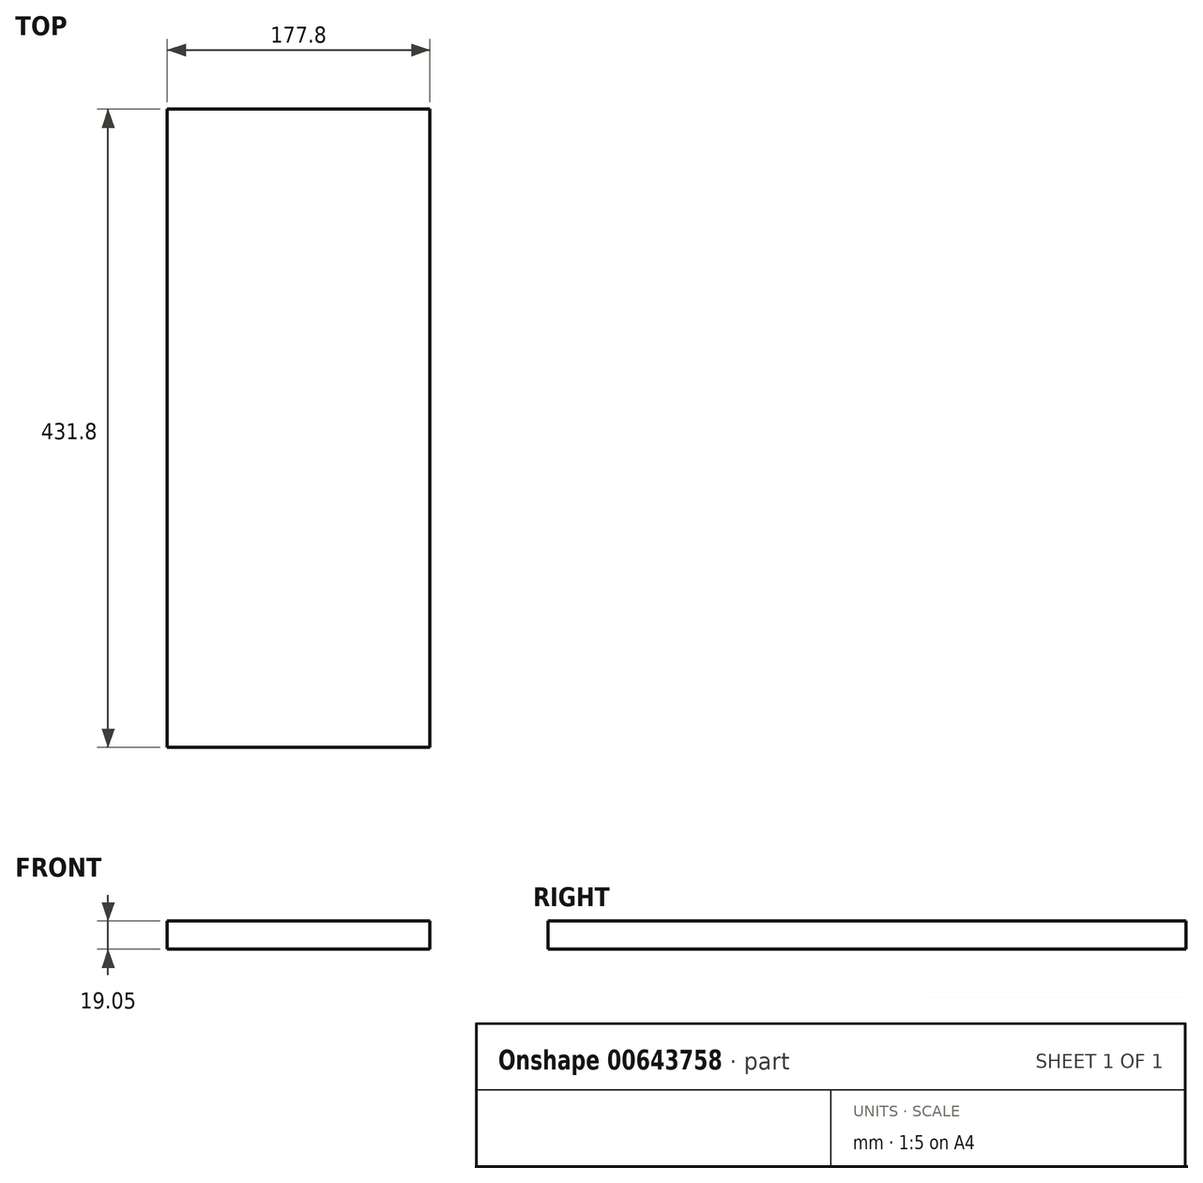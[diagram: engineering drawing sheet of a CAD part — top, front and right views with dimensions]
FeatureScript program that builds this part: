
annotation { "Feature Type Name" : "Feature", "Feature Type Description" : "" }
export const myFeature = defineFeature(function(context is Context, id is Id, definition is map)
    precondition{}
    {
        {
            var Q0;
            Q0=qCreatedBy(makeId("Top.planeOp"),FACE);
            var sketch = newSketch(context, id + "F0", { "sketchPlane" : qUnion([Q0])});
            skLineSegment(sketch, "E0.bottom", {"start": v(0, 0) * mm, "end": v(177.8, 0) * mm});
            skLineSegment(sketch, "E0.top", {"start": v(0, 431.8) * mm, "end": v(177.8, 431.8) * mm});
            skLineSegment(sketch, "E0.left", {"start": v(0, 0) * mm, "end": v(0, 431.8) * mm});
            skLineSegment(sketch, "E0.right", {"start": v(177.8, 0) * mm, "end": v(177.8, 431.8) * mm});
            skSolve(sketch);
        }
        {
            var Q0;
            Q0=makeQuery(id+"F0.imprint","IMPRINT",FACE,{"disambiguationData":[TD([[makeQuery(id+"F0.imprint","IMPRINT",EDGE,{"derivedFrom":sQuery(id+"F0.wireOp",EDGE,"E0.bottom")}),1.0]])]});
            extrude(context, id + "F1", {"entities" : qUnion([Q0]), "depth" : 19.05 * mm, "offsetDistance" : 25.4 * mm});
        }
    });
